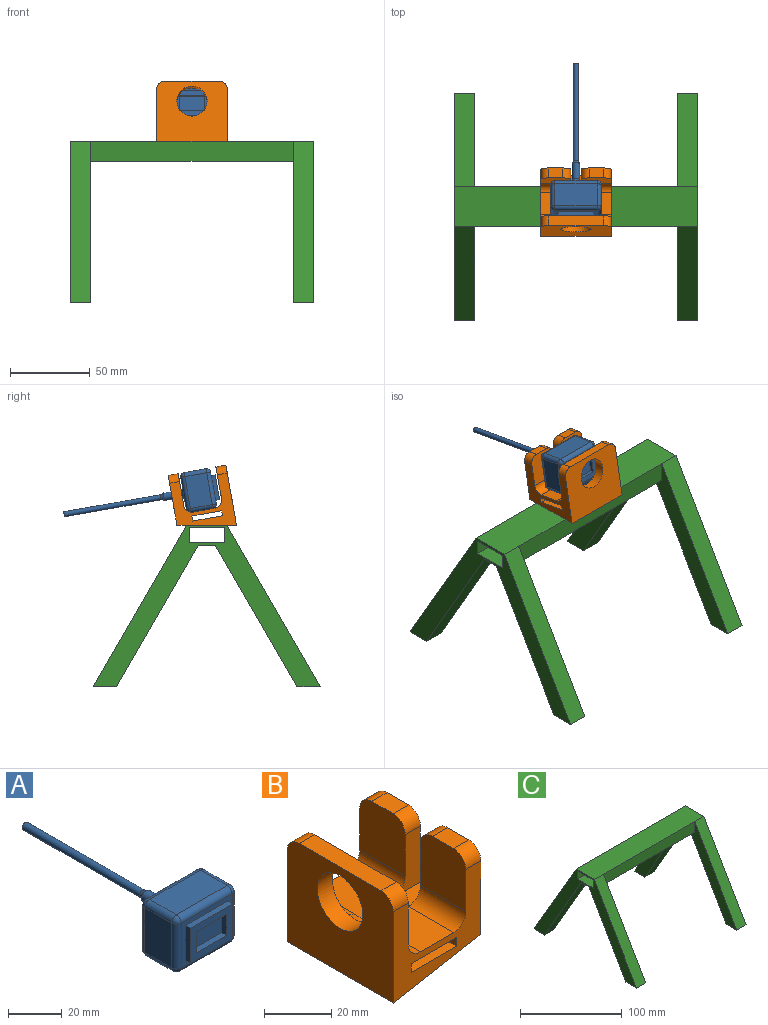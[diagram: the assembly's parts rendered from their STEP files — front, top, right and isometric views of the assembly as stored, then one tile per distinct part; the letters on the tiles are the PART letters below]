
ASSEMBLY  parts=3 mates=2
PART A: 41 faces, bbox 31.8x97.8x25.4 mm
  f0: plane 26.67x20.32mm, normal (0,-1,0), area 189.1mm2, adj f9,f10,f11,f12,f19,f20,f29,f30
  f1: plane 26.67x13.97mm, normal (0,0,1), area 372.6mm2, adj f24,f29,f32,f35
  f2: plane 20.32x13.97mm, normal (-1,0,0), area 283.9mm2, adj f21,f30,f31,f35
  f3: plane 26.67x13.97mm, normal (0,0,-1), area 372.6mm2, adj f16,f20,f21,f22
  f4: plane 20.32x13.97mm, normal (1,0,0), area 283.9mm2, adj f16,f19,f23,f24
  f5: plane 26.67x20.32mm, normal (0,1,0), area 465.8mm2, adj f22,f23,f31,f32,f39
  f6: plane 9.53x2.54mm, normal (1,0,0), area 24.2mm2, adj f7,f13,f14,f15
  f7: plane 15.88x2.54mm, normal (0,0,-1), area 40.3mm2, adj f6,f8,f14,f15
  f8: plane 9.53x2.54mm, normal (-1,0,0), area 24.2mm2, adj f7,f13,f14,f15
  f9: plane 22.23x2.54mm, normal (0,0,1), area 56.5mm2, adj f0,f10,f12,f14
  f10: plane 15.88x2.54mm, normal (-1,0,0), area 40.3mm2, adj f0,f9,f11,f14
  f11: plane 22.23x2.54mm, normal (0,0,-1), area 56.5mm2, adj f0,f10,f12,f14
  f12: plane 15.88x2.54mm, normal (1,0,0), area 40.3mm2, adj f0,f9,f11,f14
  f13: plane 15.88x2.54mm, normal (0,0,1), area 40.3mm2, adj f6,f8,f14,f15
  f14: plane 22.23x15.88mm, normal (0,-1,0), area 201.6mm2, adj f6,f7,f8,f9,f10,f11,f12,f13
  f15: plane 15.88x9.53mm, normal (0,-1,0), area 151.2mm2, adj f6,f7,f8,f13
  f16: cylinder r=2.54mm len=13.97mm, axis (0,-1,0), area 55.7mm2, adj f3,f4,f17,f18
  f17: sphere r=2.54mm, area 10.1mm2, adj f16,f19,f20
  f18: sphere r=2.54mm, area 10.1mm2, adj f16,f22,f23
  f19: cylinder r=2.54mm len=20.32mm, axis (0,0,-1), area 81.1mm2, adj f0,f4,f17,f25
  f20: cylinder r=2.54mm len=26.67mm, axis (-1,0,0), area 106.4mm2, adj f0,f3,f17,f26
  f21: cylinder r=2.54mm len=13.97mm, axis (0,1,0), area 55.7mm2, adj f2,f3,f26,f27
  f22: cylinder r=2.54mm len=26.67mm, axis (1,0,0), area 106.4mm2, adj f3,f5,f18,f27
  f23: cylinder r=2.54mm len=20.32mm, axis (0,0,1), area 81.1mm2, adj f4,f5,f18,f28
  f24: cylinder r=2.54mm len=13.97mm, axis (0,1,0), area 55.7mm2, adj f1,f4,f25,f28
  f25: sphere r=2.54mm, area 10.1mm2, adj f19,f24,f29
  f26: sphere r=2.54mm, area 10.1mm2, adj f20,f21,f30
  f27: sphere r=2.54mm, area 10.1mm2, adj f21,f22,f31
  f28: sphere r=2.54mm, area 10.1mm2, adj f23,f24,f32
  f29: cylinder r=2.54mm len=26.67mm, axis (1,0,0), area 106.4mm2, adj f0,f1,f25,f33
  f30: cylinder r=2.54mm len=20.32mm, axis (0,0,1), area 81.1mm2, adj f0,f2,f26,f33
  f31: cylinder r=2.54mm len=20.32mm, axis (0,0,-1), area 81.1mm2, adj f2,f5,f27,f34
  f32: cylinder r=2.54mm len=26.67mm, axis (-1,0,0), area 106.4mm2, adj f1,f5,f28,f34
  f33: sphere r=2.54mm, area 10.1mm2, adj f29,f30,f35
  f34: sphere r=2.54mm, area 10.1mm2, adj f31,f32,f35
  f35: cylinder r=2.54mm len=13.97mm, axis (0,-1,0), area 55.7mm2, adj f1,f2,f33,f34
  f36: cylinder r=2.38mm len=10.16mm, axis (0,-1,0), area 152mm2, adj f39,f40
  f37: plane 3.18x3.18mm, normal (0,1,0), area 7.9mm2, adj f38
  f38: cylinder r=1.59mm len=61.66mm, axis (0,-1,0), area 615mm2, adj f37,f40
  f39: torus R=4.92mm, axis (0,-1,0), area 82.8mm2, adj f5,f36
  f40: torus R=4.13mm, axis (0,-1,0), area 24.1mm2, adj f36,f38
PART B: 30 faces, bbox 36.8x44.5x38.2 mm
  f0: plane 36.83x33.16mm, normal (0,-1,0), area 562.1mm2, adj f4,f5,f6,f8,f9,f10,f18,f21
  f1: plane 36.83x33.16mm, normal (0,1,0), area 562.1mm2, adj f3,f4,f5,f6,f9,f10,f15,f19
  f2: plane 8.89x6.35mm, normal (0,0,1), area 56.5mm2, adj f3,f6,f17,f22
  f3: plane 20.32x19.05mm, normal (-1,0,0), area 376mm2, adj f1,f2,f14,f15,f17,f22
  f4: plane 44.45x38.24mm, normal (-1,0,0), area 1403.9mm2, adj f0,f1,f5,f11,f12,f23,f25
  f5: plane 44.45x36.83mm, normal (0.17,0,-0.98), area 1662.3mm2, adj f0,f1,f4,f6
  f6: plane 44.45x31.75mm, normal (1,0,0), area 1227.8mm2, adj f0,f1,f2,f5,f7,f9,f13,f14
  f7: plane 8.89x6.35mm, normal (0,0,1), area 56.5mm2, adj f6,f8,f16,f24
  f8: plane 20.32x19.05mm, normal (-1,0,0), area 376mm2, adj f0,f7,f13,f16,f18,f24
  f9: plane 44.45x25.77mm, normal (0,0,1), area 695.7mm2, adj f0,f1,f6,f13,f14,f15,f18,f19
  f10: plane 44.45x20.32mm, normal (1,0,0), area 622mm2, adj f0,f1,f11,f12,f19,f21,f23,f25
  f11: plane 34.29x6.35mm, normal (0,0,1), area 217.7mm2, adj f4,f10,f23,f25
  f12: cylinder r=9.53mm len=19.05mm, axis (-1,0,0), area 380mm2, adj f4,f10,f20
  f13: plane 20.32x11.43mm, normal (0,1,0), area 134.6mm2, adj f6,f8,f9,f16,f18
  f14: plane 20.32x11.43mm, normal (0,-1,0), area 134.6mm2, adj f3,f6,f9,f15,f17
  f15: cylinder r=5.08mm len=19.05mm, axis (0,-1,0), area 152mm2, adj f1,f3,f9,f14
  f16: cylinder r=5.08mm len=6.35mm, axis (-1,0,0), area 50.7mm2, adj f6,f7,f8,f13
  f17: cylinder r=5.08mm len=6.35mm, axis (1,0,0), area 50.7mm2, adj f2,f3,f6,f14
  f18: cylinder r=5.08mm len=19.05mm, axis (0,-1,0), area 152mm2, adj f0,f8,f9,f13
  f19: cylinder r=5.08mm len=16.51mm, axis (0,-1,0), area 131.7mm2, adj f1,f9,f10,f20
  f20: bspline ~11.43x5.08mm, area 76.3mm2, adj f9,f12,f19,f21
  f21: cylinder r=5.08mm len=16.51mm, axis (0,-1,0), area 131.7mm2, adj f0,f9,f10,f20
  f22: cylinder r=5.08mm len=6.35mm, axis (-1,0,0), area 50.7mm2, adj f1,f2,f3,f6
  f23: cylinder r=5.08mm len=6.35mm, axis (-1,0,0), area 50.7mm2, adj f1,f4,f10,f11
  f24: cylinder r=5.08mm len=6.35mm, axis (1,0,0), area 50.7mm2, adj f0,f6,f7,f8
  f25: cylinder r=5.08mm len=6.35mm, axis (1,0,0), area 50.7mm2, adj f0,f4,f10,f11
  f26: plane 44.45x3.18mm, normal (1,0,0), area 141.1mm2, adj f0,f1,f27,f29
  f27: plane 44.45x19.05mm, normal (0,0,1), area 846.8mm2, adj f0,f1,f26,f28
  f28: plane 44.45x3.18mm, normal (-1,0,0), area 141.1mm2, adj f0,f1,f27,f29
  f29: plane 44.45x19.05mm, normal (0,0,-1), area 846.8mm2, adj f0,f1,f26,f28
PART C: 50 faces, bbox 152.4x142.7x101.6 mm
  f0: plane 14.66x12.7mm, normal (0,0,-1), area 81.5mm2, adj f2,f3,f4,f5,f44,f45,f46,f47
  f1: plane 14.66x12.7mm, normal (0,0,-1), area 81.5mm2, adj f5,f8,f9,f10,f38,f39,f40,f41
  f2: plane 101.6x58.66mm, normal (0,-0.87,0.5), area 1489.9mm2, adj f0,f4,f5,f16
  f3: plane 88.9x51.33mm, normal (0,0.87,-0.5), area 1303.7mm2, adj f0,f4,f5,f6
  f4: plane 101.6x65.99mm, normal (1,0,0), area 1350.3mm2, adj f0,f2,f3,f6,f7
  f5: plane 142.72x101.6mm, normal (-1,0,0), area 2811.4mm2, adj f0,f1,f2,f3,f6,f8,f9,f12
  f6: plane 152.4x25.4mm, normal (0,0,-1), area 3498.5mm2, adj f3,f4,f5,f7,f8,f10,f11,f19
  f7: plane 127x12.7mm, normal (0,-1,0), area 1612.9mm2, adj f4,f6,f16,f20
  f8: plane 88.9x51.33mm, normal (0,-0.87,-0.5), area 1303.7mm2, adj f1,f5,f6,f10
  f9: plane 101.6x58.66mm, normal (0,0.87,0.5), area 1489.9mm2, adj f1,f5,f10,f16
  f10: plane 101.6x65.99mm, normal (1,0,0), area 1350.3mm2, adj f1,f6,f8,f9,f11
  f11: plane 127x12.7mm, normal (0,1,0), area 1612.9mm2, adj f6,f10,f16,f25
  f12: plane 152.4x22.23mm, normal (0,0,-1), area 3387.1mm2, adj f5,f13,f15,f21
  f13: plane 152.4x9.53mm, normal (0,-1,0), area 1451.6mm2, adj f5,f12,f14,f21
  f14: plane 152.4x22.23mm, normal (0,0,1), area 3387.1mm2, adj f5,f13,f15,f21
  f15: plane 152.4x9.53mm, normal (0,1,0), area 1451.6mm2, adj f5,f12,f14,f21
  f16: plane 152.4x25.4mm, normal (0,0,1), area 3871mm2, adj f2,f5,f7,f9,f11,f17,f21,f24
  f17: plane 101.6x58.66mm, normal (0,-0.87,0.5), area 1489.9mm2, adj f16,f18,f20,f21
  f18: plane 14.66x12.7mm, normal (0,0,-1), area 81.5mm2, adj f17,f19,f20,f21,f32,f33,f34,f35
  f19: plane 88.9x51.33mm, normal (0,0.87,-0.5), area 1303.7mm2, adj f6,f18,f20,f21
  f20: plane 101.6x65.99mm, normal (-1,0,0), area 1350.3mm2, adj f6,f7,f17,f18,f19
  f21: plane 142.72x101.6mm, normal (1,0,0), area 2811.4mm2, adj f6,f12,f13,f14,f15,f16,f17,f18
  f22: plane 88.9x51.33mm, normal (0,-0.87,-0.5), area 1303.7mm2, adj f6,f21,f23,f25
  f23: plane 14.66x12.7mm, normal (0,0,-1), area 81.5mm2, adj f21,f22,f24,f25,f26,f27,f30,f31
  f24: plane 101.6x58.66mm, normal (0,0.87,0.5), area 1489.9mm2, adj f16,f21,f23,f25
  f25: plane 101.6x65.99mm, normal (-1,0,0), area 1350.3mm2, adj f6,f11,f22,f23,f24
  f26: plane 98.43x62.33mm, normal (1,0,0), area 1004mm2, adj f23,f28,f29,f30,f31
  f27: plane 98.43x62.33mm, normal (-1,0,0), area 1004mm2, adj f23,f28,f29,f30,f31
  f28: plane 9.53x9.53mm, normal (0,1,0), area 90.7mm2, adj f26,f27,f29,f31
  f29: plane 9.53x5.5mm, normal (0,0,-1), area 52.4mm2, adj f26,f27,f28,f30
  f30: plane 88.9x51.33mm, normal (0,0.87,0.5), area 977.8mm2, adj f23,f26,f27,f29
  f31: plane 98.43x56.83mm, normal (0,-0.87,-0.5), area 1082.5mm2, adj f23,f26,f27,f28
  f32: plane 98.43x62.33mm, normal (-1,0,0), area 1004mm2, adj f18,f34,f35,f36,f37
  f33: plane 98.43x62.33mm, normal (1,0,0), area 1004mm2, adj f18,f34,f35,f36,f37
  f34: plane 88.9x51.33mm, normal (0,-0.87,0.5), area 977.8mm2, adj f18,f32,f33,f37
  f35: plane 98.43x56.83mm, normal (0,0.87,-0.5), area 1082.5mm2, adj f18,f32,f33,f36
  f36: plane 9.53x9.53mm, normal (0,-1,0), area 90.7mm2, adj f32,f33,f35,f37
  f37: plane 9.53x5.5mm, normal (0,0,-1), area 52.4mm2, adj f32,f33,f34,f36
  f38: plane 98.43x62.33mm, normal (-1,0,0), area 1004mm2, adj f1,f39,f40,f42,f43
  f39: plane 98.43x56.83mm, normal (0,-0.87,-0.5), area 1082.5mm2, adj f1,f38,f41,f42
  f40: plane 88.9x51.33mm, normal (0,0.87,0.5), area 977.8mm2, adj f1,f38,f41,f43
  f41: plane 98.43x62.33mm, normal (1,0,0), area 1004mm2, adj f1,f39,f40,f42,f43
  f42: plane 9.53x9.53mm, normal (0,1,0), area 90.7mm2, adj f38,f39,f41,f43
  f43: plane 9.53x5.5mm, normal (0,0,-1), area 52.4mm2, adj f38,f40,f41,f42
  f44: plane 98.43x62.33mm, normal (-1,0,0), area 1004mm2, adj f0,f45,f46,f48,f49
  f45: plane 88.9x51.33mm, normal (0,-0.87,0.5), area 977.8mm2, adj f0,f44,f47,f48
  f46: plane 98.43x56.83mm, normal (0,0.87,-0.5), area 1082.5mm2, adj f0,f44,f47,f49
  f47: plane 98.43x62.33mm, normal (1,0,0), area 1004mm2, adj f0,f45,f46,f48,f49
  f48: plane 9.53x5.5mm, normal (0,0,-1), area 52.4mm2, adj f44,f45,f47,f49
  f49: plane 9.53x9.53mm, normal (0,-1,0), area 90.7mm2, adj f44,f46,f47,f48
PLACE A rot(axis=(-1,0,0),10deg) t=(58.86,23.4,35.28)mm
PLACE B rot(axis=(-0.09,0.09,0.99),90.4deg) t=(52.51,-12.04,2.7)mm
PLACE C t=(-1.47,6.66,2.7)mm
MATE fastened B.f5 <-> C.f16  axis (0,0,-1) through (74.73,6.66,2.7)mm
MATE fastened A.f3 <-> B.f9  axis (0,-0.17,-0.98) through (74.73,9.61,11.92)mm
